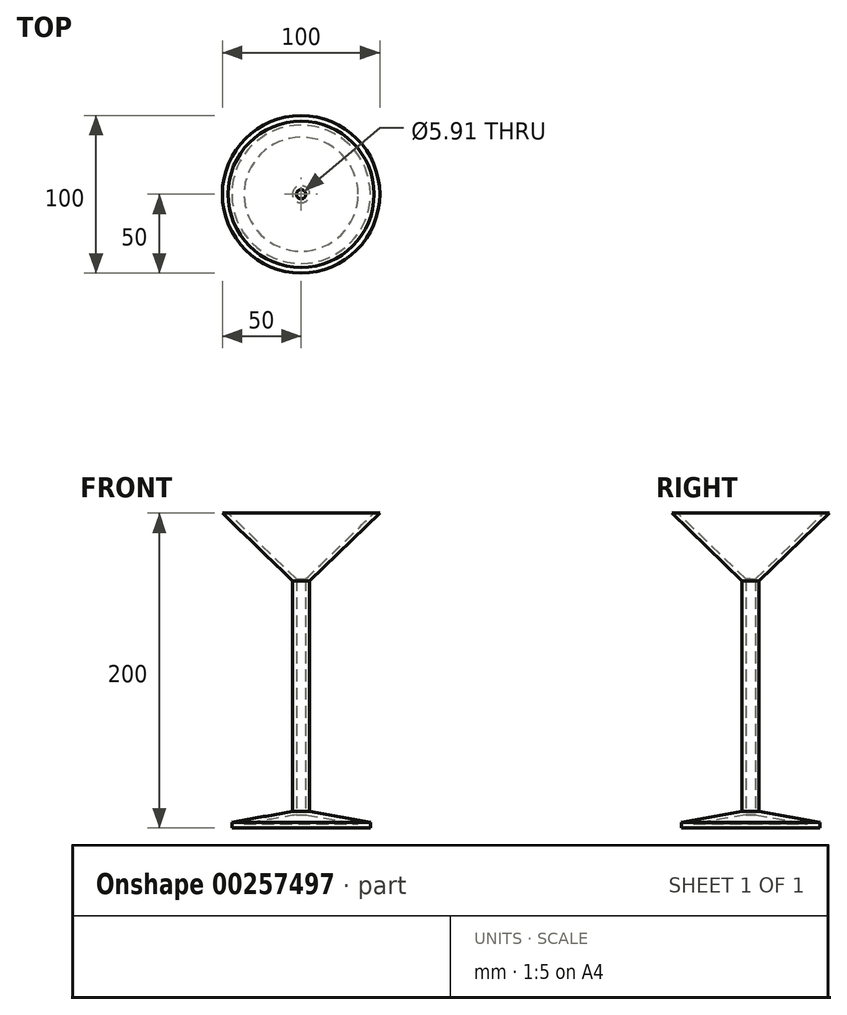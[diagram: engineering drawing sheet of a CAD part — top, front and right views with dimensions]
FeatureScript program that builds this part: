
annotation { "Feature Type Name" : "Feature", "Feature Type Description" : "" }
export const myFeature = defineFeature(function(context is Context, id is Id, definition is map)
    precondition{}
    {
        {
            var Q0;
            Q0=qCreatedBy(makeId("Front.planeOp"),FACE);
            var sketch = newSketch(context, id + "F0", { "sketchPlane" : qUnion([Q0])});
            skLineSegment(sketch, "E0", {"start": v(0, -101.18) * mm, "end": v(0, 98.82) * mm});
            skLineSegment(sketch, "E1", {"start": v(0, -101.18) * mm, "end": v(50, -101.18) * mm});
            skLineSegment(sketch, "E2", {"start": v(50, 98.82) * mm, "end": v(0, 98.82) * mm});
            skLineSegment(sketch, "E3", {"start": v(43.97, -101.18) * mm, "end": v(43.97, -97.5) * mm});
            skLineSegment(sketch, "E4", {"start": v(43.97, -97.5) * mm, "end": v(5.45, -90.75) * mm});
            skLineSegment(sketch, "E5", {"start": v(5.45, -90.75) * mm, "end": v(5.45, 55.8) * mm});
            skLineSegment(sketch, "E6", {"start": v(5.45, 55.8) * mm, "end": v(50, 98.82) * mm});
            skSolve(sketch);
        }
        {
            var Q0;
            {var subQ2=sQuery(id+"F0.wireOp",EDGE,"E0");Q0=makeQuery(id+"F0.imprint","IMPRINT",FACE,{"disambiguationData":[TD([[makeQuery(id+"F0.imprint","IMPRINT",EDGE,{"derivedFrom":subQ2}),-1.0]])]});}
            var Q1;
            Q1=sQuery(id+"F0.wireOp",EDGE,"E0");
            revolve(context, id + "F1", {"entities" : qUnion([Q0]), "axis" : qUnion([Q1]), "revolveType" : RevolveType.FULL});
        }
        {
            var Q0;
            Q0=makeQuery(id+"F1.opRevolve","SWEPT_FACE",FACE,{"disambiguationData":[OSD([sQuery(id+"F0.wireOp",EDGE,"E2")])]});
            shell(context, id + "F2", {"entities" : qUnion([Q0]), "thickness" : 2.5 * mm});
        }
    });
